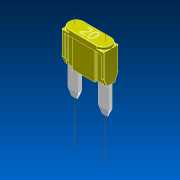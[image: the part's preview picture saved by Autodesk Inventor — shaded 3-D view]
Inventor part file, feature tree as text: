
AUTODESK INVENTOR PART (.ipt)
format: ipt  version: 2012 SP2 (Build 160219200, 219)  size: 566,784 bytes
history: native  units: mm
features: chamfer x8, other x7, sketch x7, extrude x5, mirror x2, fillet x1
ambient origin geometry x8: Origin, YZ Plane, XZ Plane, XY Plane, X Axis, Y Axis, Z Axis, Center Point
feature tree (30):
  other  "Corpo"
  extrude  "Corpo Estrusione1"  Depth=10.9mm
  extrude  "Corpo Estrusione2"  Depth=3.8mm
  extrude  "Corpo Estrusione3"  Depth=8.8mm TaperAngle=0.0deg
  extrude  "Corpo Estrusione4"  Depth=2.8mm
  mirror  "Corpo Specchio1"
  mirror  "Corpo Specchio2"
  fillet  "Corpo Raccordo1"  Radius=0.81mm
  extrude  "Pin Estrusione"  Depth=10.7mm
  chamfer  "Pin Smusso1"  Distance=7.5mm
  chamfer  "Pin Smusso2"  Distance=0.7mm
  chamfer  "Pin Smusso3"  Distance=0.7mm
  chamfer  "Pin Smusso4"  Distance=0.7mm
  chamfer  "Pin Smusso5"  Distance=0.7mm
  chamfer  "Pin Smusso6"  Distance=0.3mm
  chamfer  "Pin Smusso7"  Distance=0.3mm
  chamfer  "Pin Smusso8"  Distance=0.3mm
  sketch  "Schizzo4"
  other  "Sbalzo1"
  other  "Asse di lavoro1"
  other  "Asse di lavoro2"
  sketch  "Schizzo1"
  sketch  "Schizzo2"
  other  "Pin"
  sketch  "Schizzo3"
  other  "Linea chiusa proiettata1"
  other  "Linea chiusa proiettata2"
  sketch  "Schizzo5"
  sketch  "Schizzo6"
  sketch  "Schizzo7"
